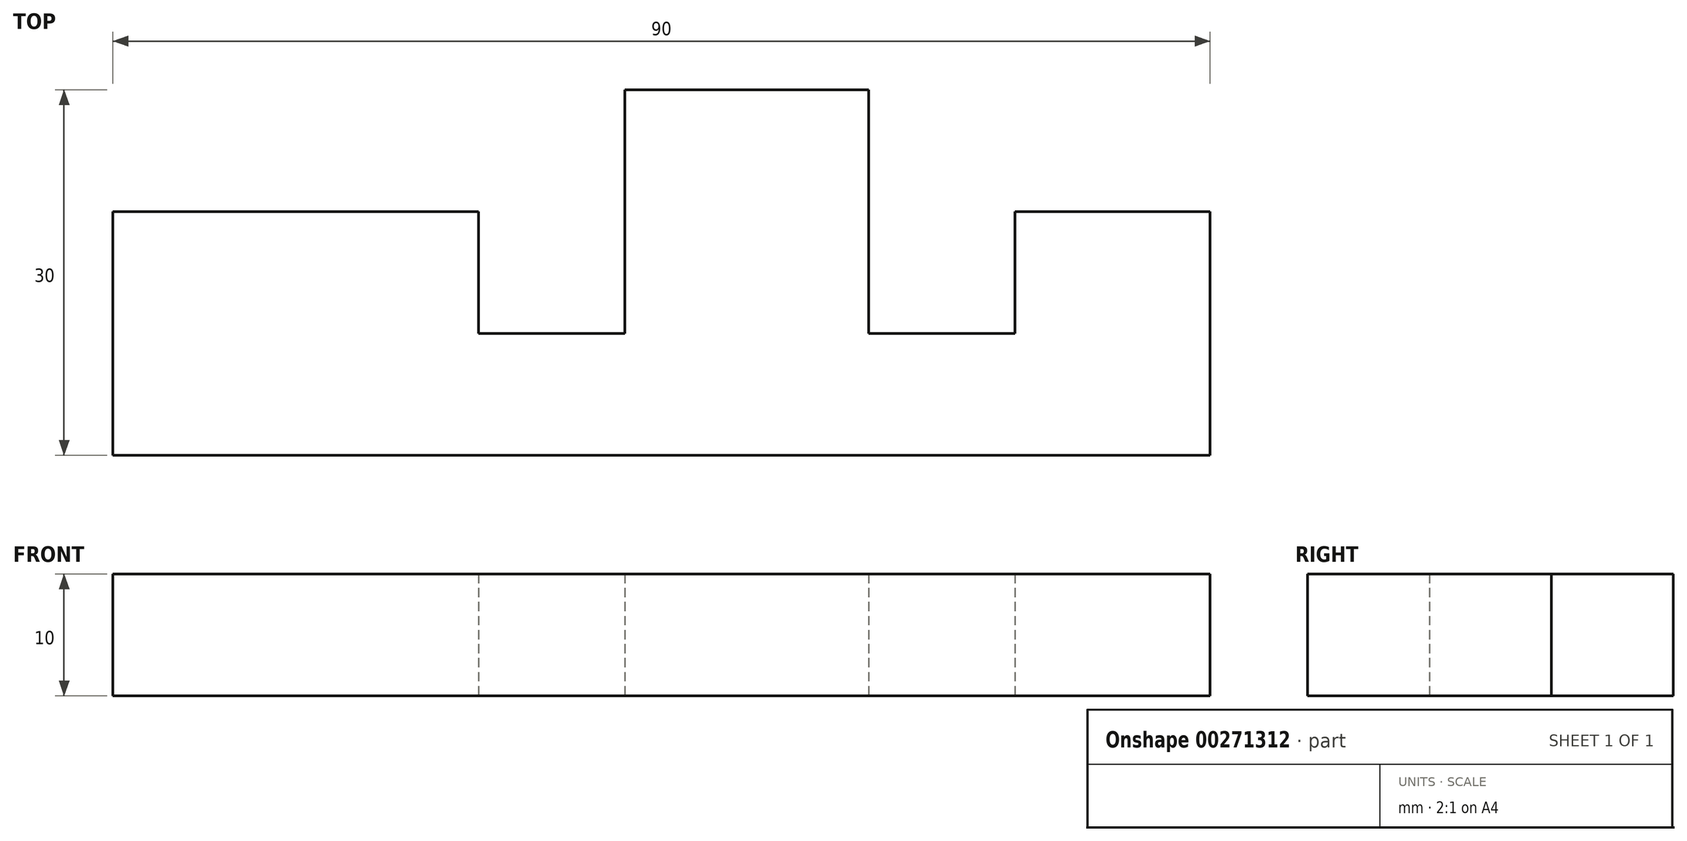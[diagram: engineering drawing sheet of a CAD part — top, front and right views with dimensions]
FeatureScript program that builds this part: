
annotation { "Feature Type Name" : "Feature", "Feature Type Description" : "" }
export const myFeature = defineFeature(function(context is Context, id is Id, definition is map)
    precondition{}
    {
        {
            var Q0;
            Q0=qCreatedBy(makeId("Top.planeOp"),FACE);
            var sketch = newSketch(context, id + "F0", { "sketchPlane" : qUnion([Q0])});
            skLineSegment(sketch, "E0.bottom", {"start": v(0, 0) * mm, "end": v(90, 0) * mm});
            skLineSegment(sketch, "E0.top", {"start": v(42, 30) * mm, "end": v(62, 30) * mm});
            skLineSegment(sketch, "E0.left", {"start": v(0, 0) * mm, "end": v(0, 20) * mm});
            skLineSegment(sketch, "E0.right", {"start": v(90, 0) * mm, "end": v(90, 20) * mm});
            skLineSegment(sketch, "E1", {"start": v(0, 20) * mm, "end": v(30, 20) * mm});
            skLineSegment(sketch, "E2", {"start": v(30, 10) * mm, "end": v(42, 10) * mm});
            skPoint(sketch, "E3", {"position": v(42, 30) * mm});
            skPoint(sketch, "E4", {"position": v(62, 30) * mm});
            skLineSegment(sketch, "E5", {"start": v(42, 30) * mm, "end": v(42, 20) * mm});
            skLineSegment(sketch, "E6", {"start": v(62, 30) * mm, "end": v(62, 20) * mm});
            skLineSegment(sketch, "E7.trimOffspring", {"start": v(74, 20) * mm, "end": v(90, 20) * mm});
            skPoint(sketch, "E8", {"position": v(30, 20) * mm});
            skLineSegment(sketch, "E9", {"start": v(42, 20) * mm, "end": v(42, 10) * mm});
            skPoint(sketch, "E10", {"position": v(74, 20) * mm});
            skLineSegment(sketch, "E11", {"start": v(74, 20) * mm, "end": v(74, 10) * mm});
            skLineSegment(sketch, "E12", {"start": v(62, 20) * mm, "end": v(62, 10) * mm});
            skLineSegment(sketch, "E13", {"start": v(30, 20) * mm, "end": v(30, 10) * mm});
            skLineSegment(sketch, "E14.trimOffspring", {"start": v(62, 10) * mm, "end": v(74, 10) * mm});
            skSolve(sketch);
        }
        {
            var Q0;
            Q0 = qSketchRegion(id + "F0", true);
            extrude(context, id + "F1", {"entities" : qUnion([Q0]), "depth" : 10 * mm});
        }
    });
